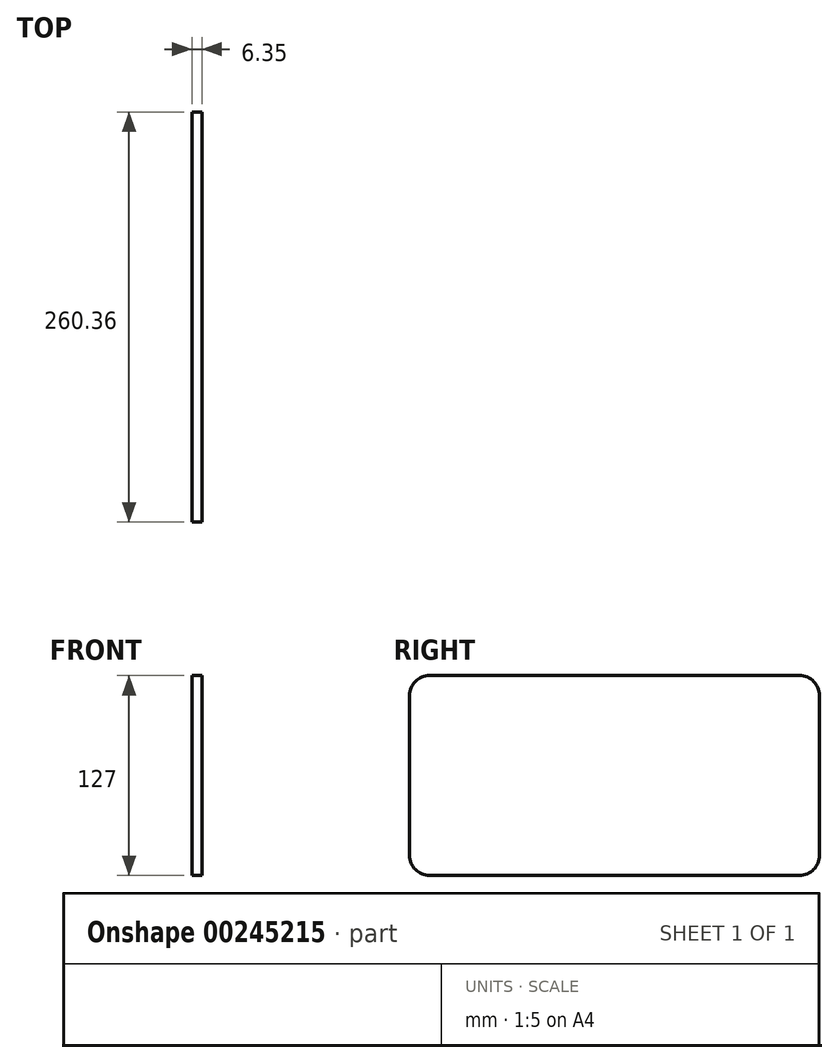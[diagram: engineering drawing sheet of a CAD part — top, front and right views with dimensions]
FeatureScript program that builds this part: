
annotation { "Feature Type Name" : "Feature", "Feature Type Description" : "" }
export const myFeature = defineFeature(function(context is Context, id is Id, definition is map)
    precondition{}
    {
        {
            var Q0;
            Q0=qCreatedBy(makeId("Right.planeOp"),FACE);
            var sketch = newSketch(context, id + "F0", { "sketchPlane" : qUnion([Q0])});
            skLineSegment(sketch, "E0.bottom", {"start": v(-117.48, 63.5) * mm, "end": v(117.48, 63.5) * mm});
            skLineSegment(sketch, "E0.top", {"start": v(-117.48, -63.5) * mm, "end": v(117.47, -63.5) * mm});
            skLineSegment(sketch, "E0.left", {"start": v(-130.18, 50.8) * mm, "end": v(-130.18, -50.8) * mm});
            skLineSegment(sketch, "E0.right", {"start": v(130.18, 50.8) * mm, "end": v(130.17, -50.8) * mm});
            skPoint(sketch, "E0.middle", {"position": v(0, 0) * mm});
            skPoint(sketch, "E1.visualSharp", {"position": v(-130.18, 63.5) * mm});
            skArc(sketch, "E1.filletArc", {"start": v(-117.48, 63.5) * mm, "mid": v(-126.46, 59.78) * mm, "end": v(-130.18, 50.8) * mm});
            skPoint(sketch, "E2.visualSharp", {"position": v(-130.18, -63.5) * mm});
            skArc(sketch, "E2.filletArc", {"start": v(-130.18, -50.8) * mm, "mid": v(-126.46, -59.78) * mm, "end": v(-117.48, -63.5) * mm});
            skPoint(sketch, "E3.visualSharp", {"position": v(130.18, 63.5) * mm});
            skArc(sketch, "E3.filletArc", {"start": v(130.18, 50.8) * mm, "mid": v(126.46, 59.78) * mm, "end": v(117.48, 63.5) * mm});
            skPoint(sketch, "E4.visualSharp", {"position": v(130.17, -63.5) * mm});
            skArc(sketch, "E4.filletArc", {"start": v(117.47, -63.5) * mm, "mid": v(126.46, -59.78) * mm, "end": v(130.17, -50.8) * mm});
            skSolve(sketch);
        }
        {
            var Q0;
            Q0=makeQuery(id+"F0.imprint","IMPRINT",FACE,{"disambiguationData":[TD([[makeQuery(id+"F0.imprint","IMPRINT",EDGE,{"derivedFrom":sQuery(id+"F0.wireOp",EDGE,"E0.bottom")}),-1.0]])]});
            extrude(context, id + "F1", {"entities" : qUnion([Q0]), "depth" : 6.35 * mm});
        }
    });
